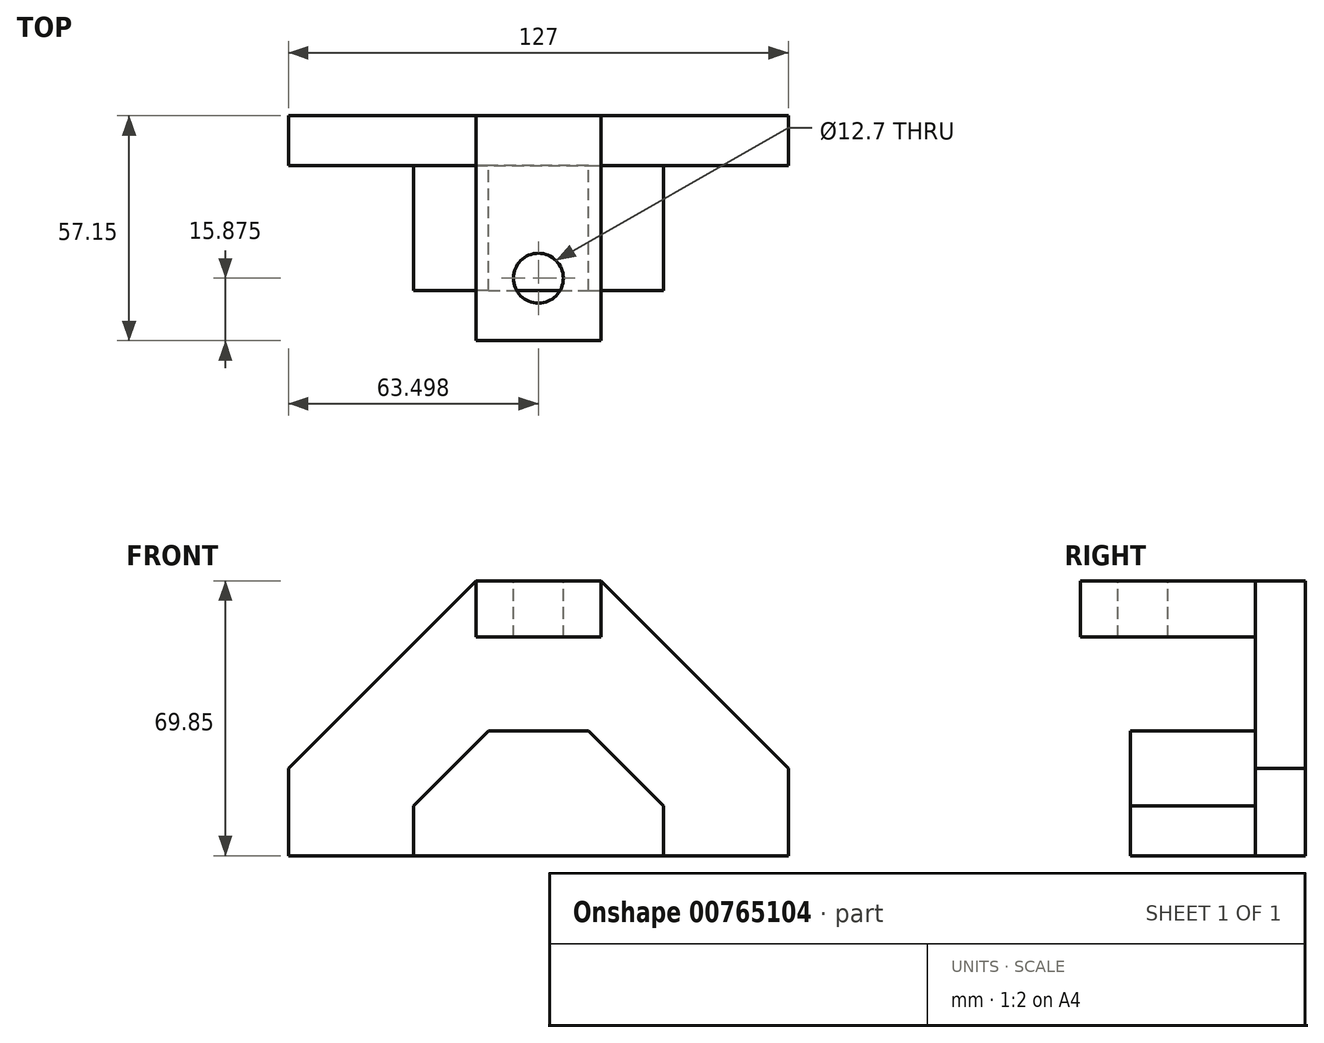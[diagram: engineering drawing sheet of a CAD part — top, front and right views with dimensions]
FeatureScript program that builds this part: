
annotation { "Feature Type Name" : "Feature", "Feature Type Description" : "" }
export const myFeature = defineFeature(function(context is Context, id is Id, definition is map)
    precondition{}
    {
        {
            var Q0;
            Q0=qCreatedBy(makeId("Front.planeOp"),FACE);
            var sketch = newSketch(context, id + "F0", { "sketchPlane" : qUnion([Q0])});
            skLineSegment(sketch, "E0", {"start": v(61.79, -41.94) * mm, "end": v(61.79, -19.72) * mm});
            skLineSegment(sketch, "E1", {"start": v(14.16, 27.9) * mm, "end": v(-17.59, 27.9) * mm});
            skLineSegment(sketch, "E2", {"start": v(14.16, 27.9) * mm, "end": v(61.79, -19.72) * mm});
            skLineSegment(sketch, "E3", {"start": v(-17.59, 27.9) * mm, "end": v(-65.21, -19.72) * mm});
            skLineSegment(sketch, "E4", {"start": v(-65.21, -41.94) * mm, "end": v(-65.21, -19.72) * mm});
            skLineSegment(sketch, "E5", {"start": v(-65.21, -41.94) * mm, "end": v(-33.46, -41.94) * mm});
            skLineSegment(sketch, "E6", {"start": v(61.79, -41.94) * mm, "end": v(30.04, -41.94) * mm});
            skLineSegment(sketch, "E7", {"start": v(30.04, -41.94) * mm, "end": v(-33.46, -41.94) * mm});
            skLineSegment(sketch, "E8", {"start": v(-33.46, -41.94) * mm, "end": v(-33.46, -29.24) * mm});
            skLineSegment(sketch, "E9", {"start": v(30.04, -41.94) * mm, "end": v(30.04, -29.24) * mm});
            skLineSegment(sketch, "E10", {"start": v(-1.71, -10.2) * mm, "end": v(10.99, -10.2) * mm});
            skLineSegment(sketch, "E11", {"start": v(10.99, -10.2) * mm, "end": v(-14.41, -10.2) * mm});
            skLineSegment(sketch, "E12", {"start": v(-14.41, -10.2) * mm, "end": v(-33.46, -29.24) * mm});
            skLineSegment(sketch, "E13", {"start": v(10.99, -10.2) * mm, "end": v(30.04, -29.24) * mm});
            skSolve(sketch);
        }
        {
            var Q0;
            Q0=makeQuery(id+"F0.imprint","IMPRINT",FACE,{"disambiguationData":[TD([[makeQuery(id+"F0.imprint","IMPRINT",EDGE,{"derivedFrom":sQuery(id+"F0.wireOp",EDGE,"E0")}),1.0]])]});
            extrude(context, id + "F1", {"entities" : qUnion([Q0]), "depth" : 12.7 * mm, "offsetDistance" : 25.4 * mm});
        }
        {
            var Q0;
            Q0=makeQuery(id+"F0.imprint","IMPRINT",FACE,{"disambiguationData":[TD([[makeQuery(id+"F0.imprint","IMPRINT",EDGE,{"derivedFrom":sQuery(id+"F0.wireOp",EDGE,"E7")}),-1.0]])]});
            extrude(context, id + "F2", {"entities" : qUnion([Q0]), "operationType" : NewBodyOperationType.ADD, "depth" : 44.45 * mm, "offsetDistance" : 25.4 * mm});
        }
        {
            var Q0;
            Q0=makeQuery(id+"F1.opExtrude","CAP_FACE",FACE,{"disambiguationData":[OSD([sQuery(id+"F0.wireOp",EDGE,"E0"),sQuery(id+"F0.wireOp",EDGE,"E1"),sQuery(id+"F0.wireOp",EDGE,"E2"),sQuery(id+"F0.wireOp",EDGE,"E3"),sQuery(id+"F0.wireOp",EDGE,"E4"),sQuery(id+"F0.wireOp",EDGE,"E5"),sQuery(id+"F0.wireOp",EDGE,"E6"),sQuery(id+"F0.wireOp",EDGE,"E8"),sQuery(id+"F0.wireOp",EDGE,"E9"),sQuery(id+"F0.wireOp",EDGE,"E11"),sQuery(id+"F0.wireOp",EDGE,"E12"),sQuery(id+"F0.wireOp",EDGE,"E13")])],"isStart":false});
            var sketch = newSketch(context, id + "F3", { "sketchPlane" : qUnion([Q0])});
            skLineSegment(sketch, "E14", {"start": v(-17.59, 27.9) * mm, "end": v(-17.59, 13.62) * mm});
            skLineSegment(sketch, "E15", {"start": v(-17.59, 13.62) * mm, "end": v(14.16, 13.62) * mm});
            skLineSegment(sketch, "E16", {"start": v(14.16, 13.62) * mm, "end": v(14.16, 27.9) * mm});
            skLineSegment(sketch, "E17", {"start": v(14.16, 27.9) * mm, "end": v(-17.59, 27.9) * mm});
            skSolve(sketch);
        }
        {
            var Q0;
            Q0=makeQuery(id+"F3.imprint","IMPRINT",FACE,{"disambiguationData":[TD([[makeQuery(id+"F3.imprint","IMPRINT",EDGE,{"derivedFrom":sQuery(id+"F3.wireOp",EDGE,"E14")}),1.0]])]});
            extrude(context, id + "F4", {"entities" : qUnion([Q0]), "operationType" : NewBodyOperationType.ADD, "depth" : 44.45 * mm, "offsetDistance" : 25.4 * mm});
        }
        {
            var Q0;
            Q0=makeQuery(id+"F4.boolean.opBoolean","MERGE",FACE,{"derivedFrom":[makeQuery(id+"F1.opExtrude","SWEPT_FACE",FACE,{"disambiguationData":[OSD([sQuery(id+"F0.wireOp",EDGE,"E1")])]}),makeQuery(id+"F4.opExtrude","SWEPT_FACE",FACE,{"disambiguationData":[OSD([sQuery(id+"F3.wireOp",EDGE,"E17")])]})]});
            var sketch = newSketch(context, id + "F5", { "sketchPlane" : qUnion([Q0])});
            skCircle(sketch, "E18", {"center": v(-1.71, -41.28) * mm, "radius": 6.35 * mm});
            skSolve(sketch);
        }
        {
            var Q0;
            Q0=makeQuery(id+"F5.imprint","IMPRINT",FACE,{"disambiguationData":[TD([[makeQuery(id+"F5.imprint","IMPRINT",EDGE,{"derivedFrom":sQuery(id+"F5.wireOp",EDGE,"E18")}),1.0]])]});
            extrude(context, id + "F6", {"entities" : qUnion([Q0]), "operationType" : NewBodyOperationType.REMOVE, "oppositeDirection" : true, "depth" : 25.4 * mm, "offsetDistance" : 25.4 * mm});
        }
    });
